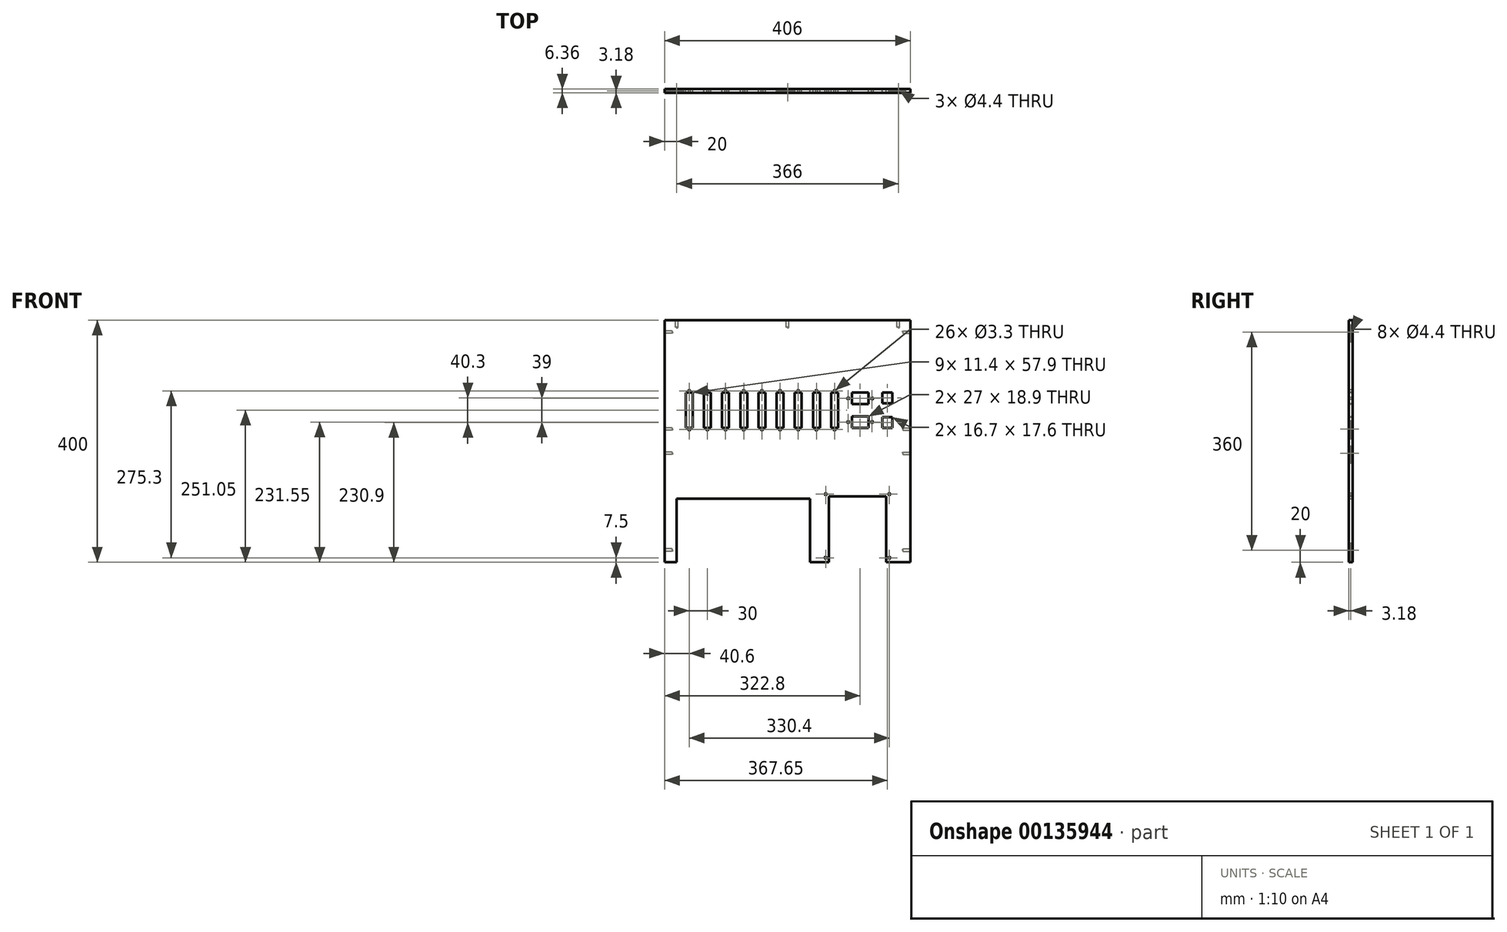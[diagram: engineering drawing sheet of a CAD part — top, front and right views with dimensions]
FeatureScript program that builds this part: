
annotation { "Feature Type Name" : "Feature", "Feature Type Description" : "" }
export const myFeature = defineFeature(function(context is Context, id is Id, definition is map)
    precondition{}
    {
        {
            var Q0;
            Q0=qCreatedBy(makeId("Front.planeOp"),FACE);
            var sketch = newSketch(context, id + "F0", { "sketchPlane" : qUnion([Q0])});
            skLineSegment(sketch, "E0.bottom", {"start": v(203, -200) * mm, "end": v(-203, -200) * mm});
            skLineSegment(sketch, "E0.top", {"start": v(203, 200) * mm, "end": v(-203, 200) * mm});
            skLineSegment(sketch, "E0.left", {"start": v(203, -200) * mm, "end": v(203, 200) * mm});
            skLineSegment(sketch, "E0.right", {"start": v(-203, -200) * mm, "end": v(-203, 200) * mm});
            skPoint(sketch, "E0.middle", {"position": v(0, 0) * mm});
            skLineSegment(sketch, "E1.bottom", {"start": v(-183, -95) * mm, "end": v(37, -95) * mm});
            skLineSegment(sketch, "E1.top", {"start": v(-183, -200) * mm, "end": v(37, -200) * mm});
            skLineSegment(sketch, "E1.left", {"start": v(-183, -95) * mm, "end": v(-183, -200) * mm});
            skLineSegment(sketch, "E1.right", {"start": v(37, -95) * mm, "end": v(37, -200) * mm});
            skLineSegment(sketch, "E2.bottom", {"start": v(68, -91.22) * mm, "end": v(163, -91.22) * mm});
            skLineSegment(sketch, "E2.top", {"start": v(68, -200) * mm, "end": v(163, -200) * mm});
            skLineSegment(sketch, "E2.left", {"start": v(68, -91.22) * mm, "end": v(68, -200) * mm});
            skLineSegment(sketch, "E2.right", {"start": v(163, -91.22) * mm, "end": v(163, -200) * mm});
            skLineSegment(sketch, "E3.bottom", {"start": v(83.3, 80) * mm, "end": v(71.9, 80) * mm});
            skLineSegment(sketch, "E3.top", {"start": v(83.3, 22.1) * mm, "end": v(71.9, 22.1) * mm});
            skLineSegment(sketch, "E3.left", {"start": v(83.3, 80) * mm, "end": v(83.3, 22.1) * mm});
            skLineSegment(sketch, "E3.right", {"start": v(71.9, 80) * mm, "end": v(71.9, 22.1) * mm});
            skLineSegment(sketch, "E4.1.0.0", {"start": v(53.3, 80) * mm, "end": v(41.9, 80) * mm});
            skLineSegment(sketch, "E4.1.0.1", {"start": v(41.9, 80) * mm, "end": v(41.9, 22.1) * mm});
            skLineSegment(sketch, "E4.1.0.2", {"start": v(53.3, 80) * mm, "end": v(53.3, 22.1) * mm});
            skLineSegment(sketch, "E4.1.0.3", {"start": v(53.3, 22.1) * mm, "end": v(41.9, 22.1) * mm});
            skLineSegment(sketch, "E4.2.0.0", {"start": v(23.3, 80) * mm, "end": v(11.9, 80) * mm});
            skLineSegment(sketch, "E4.2.0.1", {"start": v(11.9, 80) * mm, "end": v(11.9, 22.1) * mm});
            skLineSegment(sketch, "E4.2.0.2", {"start": v(23.3, 80) * mm, "end": v(23.3, 22.1) * mm});
            skLineSegment(sketch, "E4.2.0.3", {"start": v(23.3, 22.1) * mm, "end": v(11.9, 22.1) * mm});
            skLineSegment(sketch, "E4.3.0.0", {"start": v(-6.7, 80) * mm, "end": v(-18.1, 80) * mm});
            skLineSegment(sketch, "E4.3.0.1", {"start": v(-18.1, 80) * mm, "end": v(-18.1, 22.1) * mm});
            skLineSegment(sketch, "E4.3.0.2", {"start": v(-6.7, 80) * mm, "end": v(-6.7, 22.1) * mm});
            skLineSegment(sketch, "E4.3.0.3", {"start": v(-6.7, 22.1) * mm, "end": v(-18.1, 22.1) * mm});
            skLineSegment(sketch, "E4.4.0.0", {"start": v(-36.7, 80) * mm, "end": v(-48.1, 80) * mm});
            skLineSegment(sketch, "E4.4.0.1", {"start": v(-48.1, 80) * mm, "end": v(-48.1, 22.1) * mm});
            skLineSegment(sketch, "E4.4.0.2", {"start": v(-36.7, 80) * mm, "end": v(-36.7, 22.1) * mm});
            skLineSegment(sketch, "E4.4.0.3", {"start": v(-36.7, 22.1) * mm, "end": v(-48.1, 22.1) * mm});
            skLineSegment(sketch, "E4.5.0.0", {"start": v(-66.7, 80) * mm, "end": v(-78.1, 80) * mm});
            skLineSegment(sketch, "E4.5.0.1", {"start": v(-78.1, 80) * mm, "end": v(-78.1, 22.1) * mm});
            skLineSegment(sketch, "E4.5.0.2", {"start": v(-66.7, 80) * mm, "end": v(-66.7, 22.1) * mm});
            skLineSegment(sketch, "E4.5.0.3", {"start": v(-66.7, 22.1) * mm, "end": v(-78.1, 22.1) * mm});
            skLineSegment(sketch, "E4.6.0.0", {"start": v(-96.7, 80) * mm, "end": v(-108.1, 80) * mm});
            skLineSegment(sketch, "E4.6.0.1", {"start": v(-108.1, 80) * mm, "end": v(-108.1, 22.1) * mm});
            skLineSegment(sketch, "E4.6.0.2", {"start": v(-96.7, 80) * mm, "end": v(-96.7, 22.1) * mm});
            skLineSegment(sketch, "E4.6.0.3", {"start": v(-96.7, 22.1) * mm, "end": v(-108.1, 22.1) * mm});
            skLineSegment(sketch, "E4.7.0.0", {"start": v(-126.7, 80) * mm, "end": v(-138.1, 80) * mm});
            skLineSegment(sketch, "E4.7.0.1", {"start": v(-138.1, 80) * mm, "end": v(-138.1, 22.1) * mm});
            skLineSegment(sketch, "E4.7.0.2", {"start": v(-126.7, 80) * mm, "end": v(-126.7, 22.1) * mm});
            skLineSegment(sketch, "E4.7.0.3", {"start": v(-126.7, 22.1) * mm, "end": v(-138.1, 22.1) * mm});
            skLineSegment(sketch, "E4.8.0.0", {"start": v(-156.7, 80) * mm, "end": v(-168.1, 80) * mm});
            skLineSegment(sketch, "E4.8.0.1", {"start": v(-168.1, 80) * mm, "end": v(-168.1, 22.1) * mm});
            skLineSegment(sketch, "E4.8.0.2", {"start": v(-156.7, 80) * mm, "end": v(-156.7, 22.1) * mm});
            skLineSegment(sketch, "E4.8.0.3", {"start": v(-156.7, 22.1) * mm, "end": v(-168.1, 22.1) * mm});
            skLineSegment(sketch, "E4.direction1", {"start": v(71.9, 22.1) * mm, "end": v(41.9, 22.1) * mm, "construction": true});
            skLineSegment(sketch, "E5.bottom", {"start": v(133.3, 22.1) * mm, "end": v(106.3, 22.1) * mm});
            skLineSegment(sketch, "E5.top", {"start": v(133.3, 41) * mm, "end": v(106.3, 41) * mm});
            skLineSegment(sketch, "E5.left", {"start": v(133.3, 22.1) * mm, "end": v(133.3, 41) * mm});
            skLineSegment(sketch, "E5.right", {"start": v(106.3, 22.1) * mm, "end": v(106.3, 41) * mm});
            skLineSegment(sketch, "E6.0.1.0", {"start": v(133.3, 80) * mm, "end": v(106.3, 80) * mm});
            skLineSegment(sketch, "E6.0.1.1", {"start": v(106.3, 61.1) * mm, "end": v(106.3, 80) * mm});
            skLineSegment(sketch, "E6.0.1.2", {"start": v(133.3, 61.1) * mm, "end": v(106.3, 61.1) * mm});
            skLineSegment(sketch, "E6.0.1.3", {"start": v(133.3, 61.1) * mm, "end": v(133.3, 80) * mm});
            skLineSegment(sketch, "E6.direction1", {"start": v(106.3, 41) * mm, "end": v(141, 41) * mm, "construction": true});
            skLineSegment(sketch, "E6.direction2", {"start": v(106.3, 41) * mm, "end": v(106.3, 80) * mm, "construction": true});
            skLineSegment(sketch, "E7.bottom", {"start": v(156.3, 39.7) * mm, "end": v(173, 39.7) * mm});
            skLineSegment(sketch, "E7.top", {"start": v(156.3, 22.1) * mm, "end": v(173, 22.1) * mm});
            skLineSegment(sketch, "E7.left", {"start": v(156.3, 39.7) * mm, "end": v(156.3, 22.1) * mm});
            skLineSegment(sketch, "E7.right", {"start": v(173, 39.7) * mm, "end": v(173, 22.1) * mm});
            skLineSegment(sketch, "E8.0.1.0", {"start": v(156.3, 80) * mm, "end": v(173, 80) * mm});
            skLineSegment(sketch, "E8.0.1.1", {"start": v(156.3, 80) * mm, "end": v(156.3, 62.4) * mm});
            skLineSegment(sketch, "E8.0.1.2", {"start": v(156.3, 62.4) * mm, "end": v(173, 62.4) * mm});
            skLineSegment(sketch, "E8.0.1.3", {"start": v(173, 80) * mm, "end": v(173, 62.4) * mm});
            skLineSegment(sketch, "E8.direction1", {"start": v(156.3, 39.7) * mm, "end": v(191.3, 39.7) * mm, "construction": true});
            skLineSegment(sketch, "E8.direction2", {"start": v(156.3, 39.7) * mm, "end": v(156.3, 80) * mm, "construction": true});
            skSolve(sketch);
        }
        {
            var Q0;
            Q0=makeQuery(id+"F0.imprint","IMPRINT",FACE,{"disambiguationData":[TD([[makeQuery(id+"F0.imprint","IMPRINT",EDGE,{"derivedFrom":sQuery(id+"F0.wireOp",EDGE,"E0.bottom")}),-1.0]])]});
            extrude(context, id + "F1", {"entities" : qUnion([Q0]), "endBound" : BoundingType.SYMMETRIC, "depth" : 6.35 * mm});
        }
        {
            var Q0;
            Q0=makeQuery(id+"F1.opExtrude","SWEPT_FACE",FACE,{"disambiguationData":[OSD([sQuery(id+"F0.wireOp",EDGE,"E0.top")])]});
            var sketch = newSketch(context, id + "F2", { "sketchPlane" : qUnion([Q0])});
            skCircle(sketch, "E9", {"center": v(-183, 0) * mm, "radius": 2 * mm});
            skCircle(sketch, "E10", {"center": v(0, 0) * mm, "radius": 2 * mm});
            skCircle(sketch, "E11", {"center": v(183, 0) * mm, "radius": 2 * mm});
            skSolve(sketch);
        }
        {
            var Q0;
            Q0=makeQuery(id+"F1.opExtrude","SWEPT_FACE",FACE,{"disambiguationData":[OSD([sQuery(id+"F0.wireOp",EDGE,"E0.right")])]});
            var sketch = newSketch(context, id + "F3", { "sketchPlane" : qUnion([Q0])});
            skCircle(sketch, "E12", {"center": v(0, -180) * mm, "radius": 2 * mm});
            skCircle(sketch, "E13", {"center": v(0, -20) * mm, "radius": 2 * mm});
            skCircle(sketch, "E14.MirrorC", {"center": v(0, 20) * mm, "radius": 2 * mm});
            skCircle(sketch, "E15.MirrorC", {"center": v(0, 180) * mm, "radius": 2 * mm});
            skSolve(sketch);
        }
        {
            var Q0;
            Q0=makeQuery(id+"F1.opExtrude","SWEPT_FACE",FACE,{"disambiguationData":[OSD([sQuery(id+"F0.wireOp",EDGE,"E0.left")])]});
            var sketch = newSketch(context, id + "F4", { "sketchPlane" : qUnion([Q0])});
            skCircle(sketch, "E16", {"center": v(0, -180) * mm, "radius": 2 * mm});
            skCircle(sketch, "E17", {"center": v(0, -20) * mm, "radius": 2 * mm});
            skCircle(sketch, "E18.MirrorC", {"center": v(0, 180) * mm, "radius": 2 * mm});
            skCircle(sketch, "E19.MirrorC", {"center": v(0, 20) * mm, "radius": 2 * mm});
            skSolve(sketch);
        }
        {
            var Q0;
            Q0=sQuery(id+"F2.wireOp",VERTEX,"6Lffy2n0-Hwvo-p07d-KwoW-lIIL1oFBVM86.center");
            var Q1;
            Q1=sQuery(id+"F2.wireOp",VERTEX,"T9IXx7JC-zBGf-hUYm-T3yX-14epucO03qIy.center");
            var Q2;
            Q2=sQuery(id+"F2.wireOp",VERTEX,"N0LrrZqT-inZq-m3Pn-OrCf-dQQlCZNRCZq6.center");
            var Q3;
            Q3=sQuery(id+"F2.wireOp",VERTEX,"E9.center");
            var Q4;
            Q4=sQuery(id+"F2.wireOp",VERTEX,"E10.center");
            var Q5;
            Q5=sQuery(id+"F2.wireOp",VERTEX,"E11.center");
            var Q6;
            Q6=makeQuery(id+"F1.opExtrude","SWEPT_BODY",BODY,{"disambiguationData":[OSD([sQuery(id+"F0.wireOp",EDGE,"E0.bottom"),sQuery(id+"F0.wireOp",EDGE,"E0.top"),sQuery(id+"F0.wireOp",EDGE,"E0.left"),sQuery(id+"F0.wireOp",EDGE,"E0.right"),sQuery(id+"F0.wireOp",EDGE,"XWZrsFJl-hZ8c-8RFI-7IJq-EzOZ3sIGLfD4"),sQuery(id+"F0.wireOp",EDGE,"QB0C6CPn-qOL8-fIRA-QjEU-Y9BwwvSa6pRB"),sQuery(id+"F0.wireOp",EDGE,"G4GAvN2Z-Aj42-7Is6-4Fkr-iGkbHWXBV4Qq"),sQuery(id+"F0.wireOp",EDGE,"ztsScnvx-69nE-OQe9-Xu7z-F3aSEwL5bO77"),sQuery(id+"F0.wireOp",EDGE,"QAZC7S4a-mdPt-mVvo-yF0x-VzN3XJBQlE6b"),sQuery(id+"F0.wireOp",EDGE,"MX8Ww9h4-DqsU-lgLO-alZj-Cp6TfRqocJF7")])]});
            hole(context, id + "F5", {"style" : HoleStyle.SIMPLE, "endStyle" : HoleEndStyle.BLIND, "standardTappedOrClearance" : lookupTablePath({ "standard" : "ISO", "fit" : "Normal", "size" : "M4", "type" : "Clearance" }), "standardBlindInLast" : lookupTablePath({ "fit" : "Standard", "standard" : "ISO", "size" : "M4", "type" : "Clearance" }), "holeDiameter" : 4.4 * mm, "holeDepth" : 12 * mm, "locations" : qUnion([Q0, Q1, Q2, Q3, Q4, Q5]), "scope" : qUnion([Q6])});
        }
        {
            var Q0;
            Q0=sQuery(id+"F3.wireOp",VERTEX,"E12.center");
            var Q1;
            Q1=sQuery(id+"F3.wireOp",VERTEX,"qqGtBSmb-rbsb-Fcsp-kRQr-C2yqoKzzYkRx.center");
            var Q2;
            Q2=sQuery(id+"F3.wireOp",VERTEX,"np5yDtHH-8xK2-o30u-uAzj-AooPbOI2qIzy.center");
            var Q3;
            Q3=sQuery(id+"F4.wireOp",VERTEX,"96BtO6sM-U9Rg-BRqU-L3c4-5XYo4Ebyo1ly.center");
            var Q4;
            Q4=sQuery(id+"F4.wireOp",VERTEX,"eGXLnyBz-7oUu-Rtn7-jFfd-iT3XmmhfMEnJ.center");
            var Q5;
            Q5=sQuery(id+"F4.wireOp",VERTEX,"E16.center");
            var Q6;
            Q6=sQuery(id+"F4.wireOp",VERTEX,"E17.center");
            var Q7;
            Q7=sQuery(id+"F4.wireOp",VERTEX,"Qm1q9ucX-QW7I-lIMD-vBtR-auPxus0JihbM.center");
            var Q8;
            Q8=sQuery(id+"F3.wireOp",VERTEX,"5M1S5MDJ-yu4y-kJTk-Zwr1-ycYVcb5nf2MM.center");
            var Q9;
            Q9=sQuery(id+"F3.wireOp",VERTEX,"E13.center");
            var Q10;
            Q10=sQuery(id+"F4.wireOp",VERTEX,"E19.MirrorC.center");
            var Q11;
            Q11=sQuery(id+"F4.wireOp",VERTEX,"E18.MirrorC.center");
            var Q12;
            Q12=sQuery(id+"F3.wireOp",VERTEX,"E14.MirrorC.center");
            var Q13;
            Q13=sQuery(id+"F3.wireOp",VERTEX,"E15.MirrorC.center");
            var Q14;
            Q14=makeQuery(id+"F1.opExtrude","SWEPT_BODY",BODY,{"disambiguationData":[OSD([sQuery(id+"F0.wireOp",EDGE,"E0.bottom"),sQuery(id+"F0.wireOp",EDGE,"E0.top"),sQuery(id+"F0.wireOp",EDGE,"E0.left"),sQuery(id+"F0.wireOp",EDGE,"E0.right")])]});
            hole(context, id + "F6", {"style" : HoleStyle.SIMPLE, "endStyle" : HoleEndStyle.BLIND, "standardTappedOrClearance" : lookupTablePath({ "standard" : "ISO", "fit" : "Normal", "size" : "M4", "type" : "Clearance" }), "standardBlindInLast" : lookupTablePath({ "fit" : "Standard", "standard" : "ISO", "size" : "M4", "type" : "Clearance" }), "holeDiameter" : 4.4 * mm, "holeDepth" : 12 * mm, "startFromSketch" : true, "locations" : qUnion([Q0, Q1, Q2, Q3, Q4, Q5, Q6, Q7, Q8, Q9, Q10, Q11, Q12, Q13]), "scope" : qUnion([Q14])});
        }
        {
            var Q0;
            Q0=makeQuery(id+"F1.opExtrude","CAP_FACE",FACE,{"disambiguationData":[OSD([sQuery(id+"F0.wireOp",EDGE,"E0.bottom"),sQuery(id+"F0.wireOp",EDGE,"E0.top"),sQuery(id+"F0.wireOp",EDGE,"E0.left"),sQuery(id+"F0.wireOp",EDGE,"E0.right"),sQuery(id+"F0.wireOp",EDGE,"E1.bottom"),sQuery(id+"F0.wireOp",EDGE,"E1.left"),sQuery(id+"F0.wireOp",EDGE,"E1.right"),sQuery(id+"F0.wireOp",EDGE,"E2.bottom"),sQuery(id+"F0.wireOp",EDGE,"E2.left"),sQuery(id+"F0.wireOp",EDGE,"E2.right")])],"isStart":false});
            var sketch = newSketch(context, id + "F7", { "sketchPlane" : qUnion([Q0])});
            skCircle(sketch, "E20", {"center": v(168, -192.5) * mm, "radius": 2 * mm});
            skCircle(sketch, "E21", {"center": v(63, -192.5) * mm, "radius": 2 * mm});
            skCircle(sketch, "E22", {"center": v(168, -87.5) * mm, "radius": 2 * mm});
            skCircle(sketch, "E23", {"center": v(63, -87.5) * mm, "radius": 2 * mm});
            skCircle(sketch, "E24", {"center": v(77.6, 82.8) * mm, "radius": 1.5 * mm});
            skCircle(sketch, "E25.0.1.0", {"center": v(77.6, 19.3) * mm, "radius": 1.5 * mm});
            skCircle(sketch, "E25.1.0.0", {"center": v(47.6, 82.8) * mm, "radius": 1.5 * mm});
            skCircle(sketch, "E25.1.1.0", {"center": v(47.6, 19.3) * mm, "radius": 1.5 * mm});
            skCircle(sketch, "E25.2.0.0", {"center": v(17.6, 82.8) * mm, "radius": 1.5 * mm});
            skCircle(sketch, "E25.2.1.0", {"center": v(17.6, 19.3) * mm, "radius": 1.5 * mm});
            skCircle(sketch, "E25.3.0.0", {"center": v(-12.4, 82.8) * mm, "radius": 1.5 * mm});
            skCircle(sketch, "E25.3.1.0", {"center": v(-12.4, 19.3) * mm, "radius": 1.5 * mm});
            skCircle(sketch, "E25.4.0.0", {"center": v(-42.4, 82.8) * mm, "radius": 1.5 * mm});
            skCircle(sketch, "E25.4.1.0", {"center": v(-42.4, 19.3) * mm, "radius": 1.5 * mm});
            skCircle(sketch, "E25.5.0.0", {"center": v(-72.4, 82.8) * mm, "radius": 1.5 * mm});
            skCircle(sketch, "E25.5.1.0", {"center": v(-72.4, 19.3) * mm, "radius": 1.5 * mm});
            skCircle(sketch, "E25.6.0.0", {"center": v(-102.4, 82.8) * mm, "radius": 1.5 * mm});
            skCircle(sketch, "E25.6.1.0", {"center": v(-102.4, 19.3) * mm, "radius": 1.5 * mm});
            skCircle(sketch, "E25.7.0.0", {"center": v(-132.4, 82.8) * mm, "radius": 1.5 * mm});
            skCircle(sketch, "E25.7.1.0", {"center": v(-132.4, 19.3) * mm, "radius": 1.5 * mm});
            skCircle(sketch, "E25.8.0.0", {"center": v(-162.4, 82.8) * mm, "radius": 1.5 * mm});
            skCircle(sketch, "E25.8.1.0", {"center": v(-162.4, 19.3) * mm, "radius": 1.5 * mm});
            skLineSegment(sketch, "E25.direction1", {"start": v(77.6, 82.8) * mm, "end": v(47.6, 82.8) * mm, "construction": true});
            skLineSegment(sketch, "E25.direction2", {"start": v(77.6, 82.8) * mm, "end": v(77.6, 19.3) * mm, "construction": true});
            skCircle(sketch, "E26", {"center": v(139.55, 31.55) * mm, "radius": 1.2 * mm});
            skCircle(sketch, "E27.0.1.0", {"center": v(139.55, 70.55) * mm, "radius": 1.2 * mm});
            skCircle(sketch, "E27.1.0.0", {"center": v(100.05, 31.55) * mm, "radius": 1.2 * mm});
            skCircle(sketch, "E27.1.1.0", {"center": v(100.05, 70.55) * mm, "radius": 1.2 * mm});
            skLineSegment(sketch, "E27.direction1", {"start": v(139.55, 31.55) * mm, "end": v(100.05, 31.55) * mm, "construction": true});
            skLineSegment(sketch, "E27.direction2", {"start": v(139.55, 31.55) * mm, "end": v(139.55, 70.55) * mm, "construction": true});
            skSolve(sketch);
        }
        {
            var Q0;
            Q0=sQuery(id+"F7.wireOp",VERTEX,"E23.center");
            var Q1;
            Q1=sQuery(id+"F7.wireOp",VERTEX,"E22.center");
            var Q2;
            Q2=sQuery(id+"F7.wireOp",VERTEX,"E20.center");
            var Q3;
            Q3=sQuery(id+"F7.wireOp",VERTEX,"E21.center");
            var Q4;
            Q4=sQuery(id+"F7.wireOp",VERTEX,"E24.center");
            var Q5;
            Q5=sQuery(id+"F7.wireOp",VERTEX,"E25.1.0.0.center");
            var Q6;
            Q6=sQuery(id+"F7.wireOp",VERTEX,"E25.0.1.0.center");
            var Q7;
            Q7=sQuery(id+"F7.wireOp",VERTEX,"E25.1.1.0.center");
            var Q8;
            Q8=sQuery(id+"F7.wireOp",VERTEX,"E25.2.1.0.center");
            var Q9;
            Q9=sQuery(id+"F7.wireOp",VERTEX,"E25.2.0.0.center");
            var Q10;
            Q10=sQuery(id+"F7.wireOp",VERTEX,"E25.3.0.0.center");
            var Q11;
            Q11=sQuery(id+"F7.wireOp",VERTEX,"E25.3.1.0.center");
            var Q12;
            Q12=sQuery(id+"F7.wireOp",VERTEX,"E25.4.1.0.center");
            var Q13;
            Q13=sQuery(id+"F7.wireOp",VERTEX,"E25.4.0.0.center");
            var Q14;
            Q14=sQuery(id+"F7.wireOp",VERTEX,"E25.5.0.0.center");
            var Q15;
            Q15=sQuery(id+"F7.wireOp",VERTEX,"E25.5.1.0.center");
            var Q16;
            Q16=sQuery(id+"F7.wireOp",VERTEX,"E25.6.1.0.center");
            var Q17;
            Q17=sQuery(id+"F7.wireOp",VERTEX,"E25.6.0.0.center");
            var Q18;
            Q18=sQuery(id+"F7.wireOp",VERTEX,"E25.7.0.0.center");
            var Q19;
            Q19=sQuery(id+"F7.wireOp",VERTEX,"E25.7.1.0.center");
            var Q20;
            Q20=sQuery(id+"F7.wireOp",VERTEX,"E25.8.1.0.center");
            var Q21;
            Q21=sQuery(id+"F7.wireOp",VERTEX,"E25.8.0.0.center");
            var Q22;
            Q22=sQuery(id+"F7.wireOp",VERTEX,"E27.direction2.end");
            var Q23;
            Q23=sQuery(id+"F7.wireOp",VERTEX,"E27.1.1.0.center");
            var Q24;
            Q24=sQuery(id+"F7.wireOp",VERTEX,"E27.direction1.end");
            var Q25;
            Q25=sQuery(id+"F7.wireOp",VERTEX,"E26.center");
            var Q26;
            Q26=makeQuery(id+"F1.opExtrude","SWEPT_BODY",BODY,{"disambiguationData":[OSD([sQuery(id+"F0.wireOp",EDGE,"E0.bottom"),sQuery(id+"F0.wireOp",EDGE,"E0.top"),sQuery(id+"F0.wireOp",EDGE,"E0.left"),sQuery(id+"F0.wireOp",EDGE,"E0.right"),sQuery(id+"F0.wireOp",EDGE,"E1.bottom"),sQuery(id+"F0.wireOp",EDGE,"E1.left"),sQuery(id+"F0.wireOp",EDGE,"E1.right"),sQuery(id+"F0.wireOp",EDGE,"E2.bottom"),sQuery(id+"F0.wireOp",EDGE,"E2.left"),sQuery(id+"F0.wireOp",EDGE,"E2.right")])]});
            hole(context, id + "F8", {"style" : HoleStyle.SIMPLE, "endStyle" : HoleEndStyle.THROUGH, "standardTappedOrClearance" : lookupTablePath({ "standard" : "ISO", "fit" : "Normal", "size" : "M3", "type" : "Clearance" }), "standardBlindInLast" : lookupTablePath({ "fit" : "Standard", "standard" : "ISO", "size" : "M3", "type" : "Clearance" }), "holeDiameter" : 3.3 * mm, "startFromSketch" : true, "locations" : qUnion([Q0, Q1, Q2, Q3, Q4, Q5, Q6, Q7, Q8, Q9, Q10, Q11, Q12, Q13, Q14, Q15, Q16, Q17, Q18, Q19, Q20, Q21, Q22, Q23, Q24, Q25]), "scope" : qUnion([Q26]), "isTappedThrough" : true});
        }
    });
